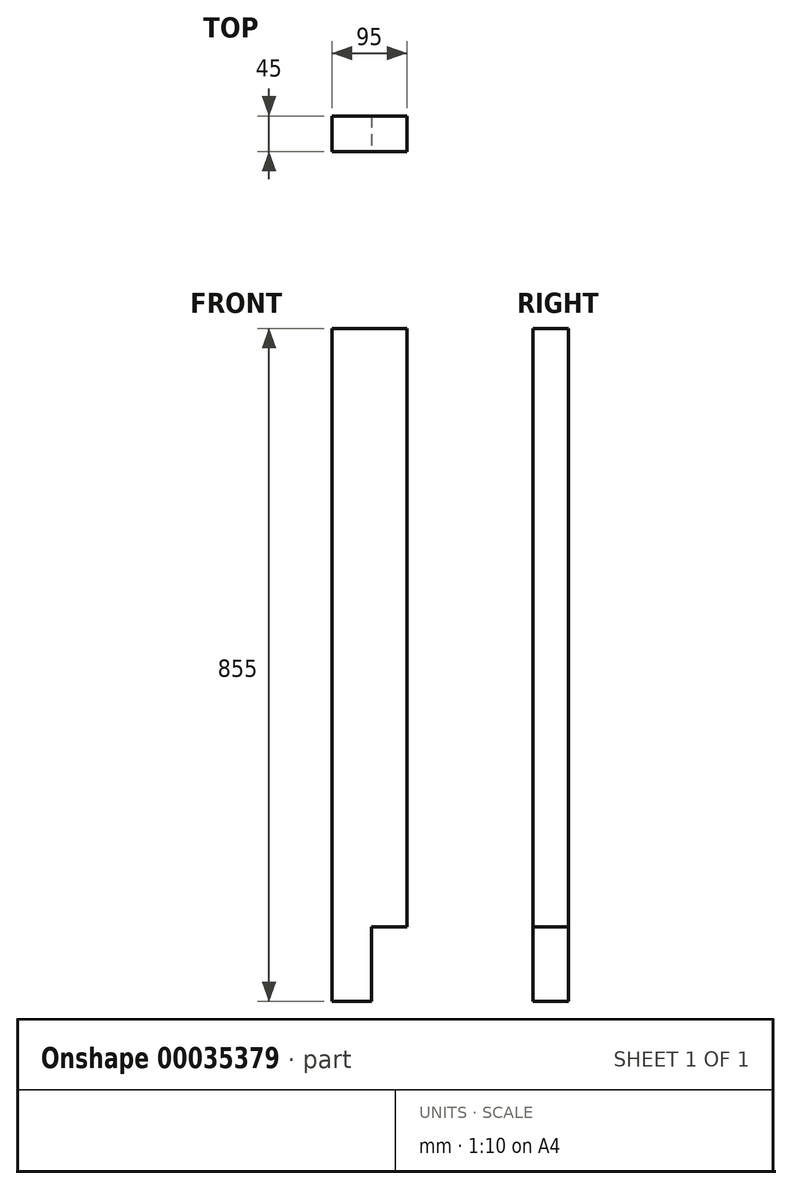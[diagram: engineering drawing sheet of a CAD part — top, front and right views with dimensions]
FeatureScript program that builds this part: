
annotation { "Feature Type Name" : "Feature", "Feature Type Description" : "" }
export const myFeature = defineFeature(function(context is Context, id is Id, definition is map)
    precondition{}
    {
        {
            var Q0;
            Q0=qCreatedBy(makeId("Top.planeOp"),FACE);
            var sketch = newSketch(context, id + "F0", { "sketchPlane" : qUnion([Q0])});
            skLineSegment(sketch, "E0.rect.bottom", {"start": v(47.5, -22.5) * mm, "end": v(-47.5, -22.5) * mm});
            skLineSegment(sketch, "E0.rect.top", {"start": v(47.5, 22.5) * mm, "end": v(-47.5, 22.5) * mm});
            skLineSegment(sketch, "E0.rect.left", {"start": v(47.5, -22.5) * mm, "end": v(47.5, 22.5) * mm});
            skLineSegment(sketch, "E0.rect.right", {"start": v(-47.5, -22.5) * mm, "end": v(-47.5, 22.5) * mm});
            skPoint(sketch, "E0.rect.middle", {"position": v(0, 0) * mm});
            skSolve(sketch);
        }
        {
            var Q0;
            Q0=makeQuery(id+"F0.imprint","IMPRINT",FACE,{"disambiguationData":[TD([[makeQuery(id+"F0.imprint","IMPRINT",EDGE,{"derivedFrom":sQuery(id+"F0.wireOp",EDGE,"E0.rect.bottom")}),-1.0]])]});
            extrude(context, id + "F1", {"entities" : qUnion([Q0]), "depth" : 855 * mm});
        }
        {
            var Q0;
            Q0=makeQuery(id+"F1.opExtrude","SWEPT_FACE",FACE,{"disambiguationData":[OSD([sQuery(id+"F0.wireOp",EDGE,"E0.rect.bottom")])]});
            var sketch = newSketch(context, id + "F2", { "sketchPlane" : qUnion([Q0])});
            skLineSegment(sketch, "E1.bottom", {"start": v(47.5, 0) * mm, "end": v(2.5, 0) * mm});
            skLineSegment(sketch, "E1.top", {"start": v(47.5, 95) * mm, "end": v(2.5, 95) * mm});
            skLineSegment(sketch, "E1.left", {"start": v(47.5, 0) * mm, "end": v(47.5, 95) * mm});
            skLineSegment(sketch, "E1.right", {"start": v(2.5, 0) * mm, "end": v(2.5, 95) * mm});
            skSolve(sketch);
        }
        {
            var Q0;
            Q0=makeQuery(id+"F2.imprint","IMPRINT",FACE,{"disambiguationData":[TD([[makeQuery(id+"F2.imprint","IMPRINT",EDGE,{"derivedFrom":sQuery(id+"F2.wireOp",EDGE,"E1.bottom")}),-1.0]])]});
            extrude(context, id + "F3", {"entities" : qUnion([Q0]), "operationType" : NewBodyOperationType.REMOVE, "endBound" : BoundingType.THROUGH_ALL, "oppositeDirection" : true, "depth" : 25 * mm});
        }
    });
